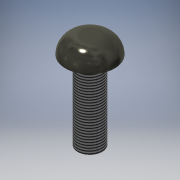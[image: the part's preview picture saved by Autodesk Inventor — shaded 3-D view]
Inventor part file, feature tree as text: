
AUTODESK INVENTOR PART (.ipt)
format: ipt  version: 2016 (Build 200138000, 138)  size: 143,360 bytes
history: native  units: mm
features: extrude x3, sketch x3, other x1, fillet x1, thread x1
ambient origin geometry x1: Origin
bodies: Body1 (feature_tree)
feature tree (9):
  other  "ソリッド1"
  extrude  "押し出し1"  Depth=5.0mm
  extrude  "押し出し2"  Depth=6.0mm TaperAngle=0.0deg
  fillet  "フィレット1"  Radius=10.0mm
  thread  "ねじ1"
  extrude  "押し出し3"  Depth=3.4mm TaperAngle=0.0deg
  sketch  "スケッチ1"
  sketch  "スケッチ2"
  sketch  "スケッチ3"
